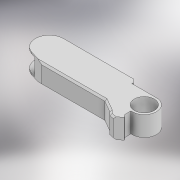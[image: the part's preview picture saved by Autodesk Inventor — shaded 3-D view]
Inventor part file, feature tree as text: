
AUTODESK INVENTOR PART (.ipt)
format: ipt  version: 2022 (Build 260153000, 153)  size: 208,896 bytes
history: native  units: mm
features: sketch x6, extrude x5, chamfer x2, plane x1, fillet x1
ambient origin geometry x8: Origin, YZ Plane, XZ Plane, XY Plane, X Axis, Y Axis, Z Axis, Center Point
bodies: Solid1 (feature_tree)
feature tree (15):
  extrude  "Extrusion1"  Depth=5.5mm
  plane  "Work Plane1"
  sketch  "Sketch2"  dims[d2=24.43461mm d3=1.5mm]
  extrude  "Extrusion2"  Depth=1.5mm
  extrude  "Extrusion3"  Depth=1.25mm
  extrude  "Extrusion4"  Depth=1.0mm
  extrude  "Extrusion5"  Depth=3.5mm
  fillet  "Fillet1"  Radius=2.0mm
  chamfer  "Chamfer1"  Distance=6.0mm
  chamfer  "Chamfer2"  Distance=5.95mm
  sketch  "Sketch1"  dims[d0=7.25mm d1=5.5mm]
  sketch  "Sketch3"  dims[d4=1.8mm d5=1.25mm]
  sketch  "Sketch4"  dims[d6=0.25mm d7=1.0mm]
  sketch  "Sketch5"  dims[d8=1.0mm d9=3.5mm d10=2.0mm]
  sketch  "Sketch6"  dims[d11=19.0mm d12=6.0mm d13=5.95mm d14=0.0mm d15=5.083mm d16=7.5mm d17=5.0mm d18=8.25mm d19=0.0mm d20=5.1mm d21=5.0mm d22=0.0mm d23=3.5mm d24=4.25mm d25=0.0mm d26=2.0mm d27=4.25mm d28=0.0mm d29=0.3665mm d30=0.5mm d31=2.0mm d32=45.0deg d33=1.0mm d34=2.0mm d35=45.0deg]
